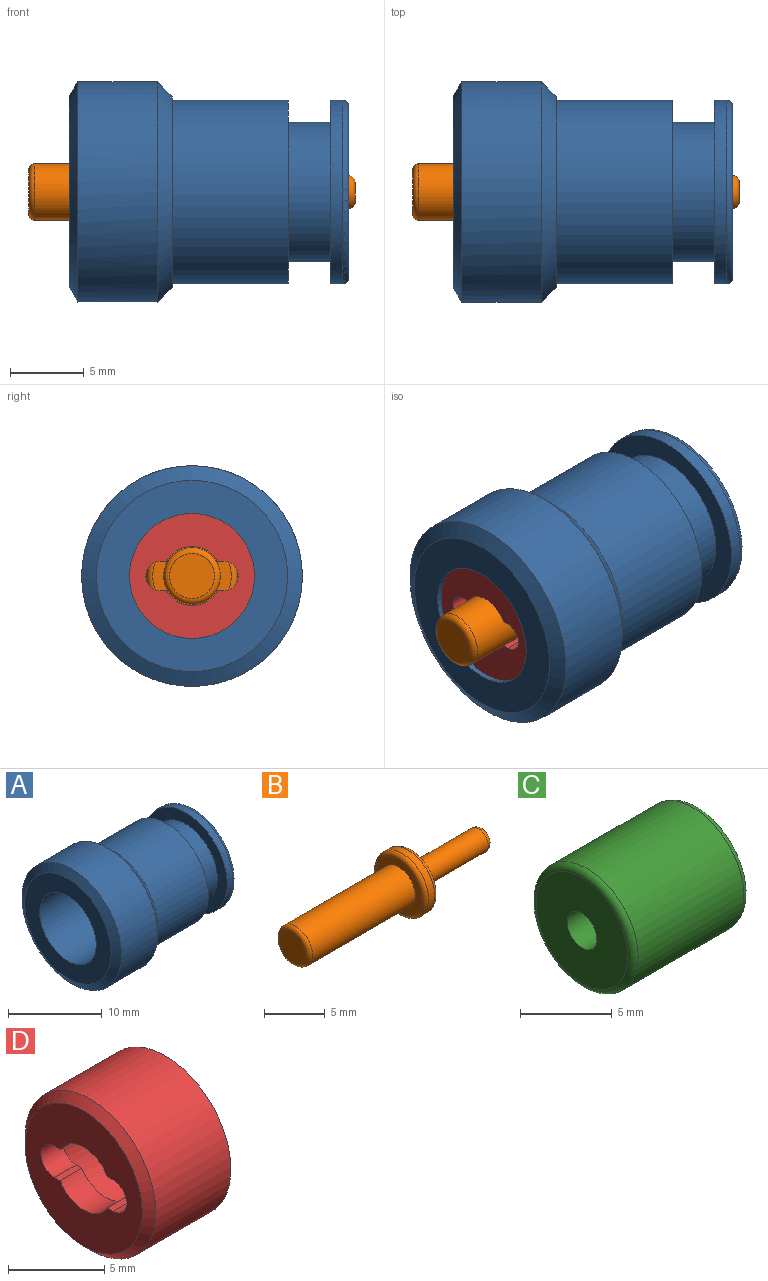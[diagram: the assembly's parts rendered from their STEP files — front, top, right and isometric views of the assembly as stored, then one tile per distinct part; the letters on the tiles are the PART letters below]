
ASSEMBLY  parts=4 mates=3
PART A: 19 faces, bbox 19x15x15 mm
  f0: plane 13x13mm, normal (-1,0,0), area 76mm2, adj f1,f16
  f1: cylinder r=4.25mm len=8.5mm, axis (-1,0,0), area 213.6mm2, adj f0,f2
  f2: plane 8.5x8.5mm, normal (-1,0,0), area 6.5mm2, adj f1,f3
  f3: cylinder r=4mm len=8mm, axis (-1,0,0), area 193.5mm2, adj f2,f4
  f4: plane 8x8mm, normal (-1,0,0), area 23.8mm2, adj f3,f5
  f5: cylinder r=2.9mm len=5.8mm, axis (-1,0,0), area 32.8mm2, adj f4,f6
  f6: plane 5.8x5.8mm, normal (-1,0,0), area 21.9mm2, adj f5,f7
  f7: cylinder r=1.2mm len=2.4mm, axis (-1,0,0), area 11.3mm2, adj f6,f8
  f8: plane 11.68x11.68mm, normal (1,0,0), area 102.5mm2, adj f7,f18
  f9: cylinder r=6.24mm len=12.48mm, axis (-1,0,0), area 33.3mm2, adj f10,f18
  f10: plane 12.48x12.48mm, normal (-1,0,0), area 51.6mm2, adj f9,f11
  f11: cylinder r=4.74mm len=9.48mm, axis (-1,0,0), area 84.9mm2, adj f10,f12
  f12: plane 12.48x12.48mm, normal (1,0,0), area 51.6mm2, adj f11,f13
  f13: cylinder r=6.24mm len=12.48mm, axis (-1,0,0), area 309.6mm2, adj f12,f14
  f14: plane 13x13mm, normal (1,0,0), area 10.5mm2, adj f13,f17
  f15: cylinder r=7.5mm len=15mm, axis (-1,0,0), area 255.5mm2, adj f16,f17
  f16: cone r=6.5mm half-angle=60deg, axis (1,0,0), area 50.8mm2, adj f0,f15
  f17: cone r=7.5mm half-angle=45deg, axis (-1,0,0), area 62.2mm2, adj f14,f15
  f18: torus R=5.84mm, axis (1,0,0), area 24.1mm2, adj f8,f9
PART B: 11 faces, bbox 22.2x6.7x6.7 mm
  f0: plane 1.27x1.27mm, normal (1,0,0), area 1.3mm2, adj f1
  f1: torus R=0.63mm, axis (1,0,0), area 4.7mm2, adj f0,f2
  f2: cylinder r=1.13mm len=7.8mm, axis (1,0,0), area 55.5mm2, adj f1,f3
  f3: plane 5.35x5.35mm, normal (1,0,0), area 18.4mm2, adj f2,f4
  f4: torus R=2.67mm, axis (1,0,0), area 11.6mm2, adj f3,f5
  f5: cylinder r=3.08mm len=6.15mm, axis (1,0,0), area 13.5mm2, adj f4,f6
  f6: torus R=2.67mm, axis (1,0,0), area 11.6mm2, adj f5,f7
  f7: plane 5.35x5.35mm, normal (-1,0,0), area 10.8mm2, adj f6,f8
  f8: cylinder r=1.93mm len=12mm, axis (1,0,0), area 145.1mm2, adj f7,f9
  f9: torus R=1.53mm, axis (1,0,0), area 7mm2, adj f8,f10
  f10: plane 3.05x3.05mm, normal (-1,0,0), area 7.3mm2, adj f9
PART C: 8 faces, bbox 8.9x8.5x8.5 mm
  f0: plane 7.05x7.05mm, normal (-1,0,0), area 34.9mm2, adj f1,f7
  f1: cylinder r=1.15mm len=2.3mm, axis (1,0,0), area 12mm2, adj f0,f2
  f2: plane 6.3x6.3mm, normal (1,0,0), area 27mm2, adj f1,f3
  f3: cylinder r=3.15mm len=7.28mm, axis (1,0,0), area 144.1mm2, adj f2,f4
  f4: plane 7.05x7.05mm, normal (1,0,0), area 7.9mm2, adj f3,f5
  f5: torus R=3.53mm, axis (1,0,0), area 14.9mm2, adj f4,f6
  f6: cylinder r=3.93mm len=8.14mm, axis (1,0,0), area 200.8mm2, adj f5,f7
  f7: torus R=3.53mm, axis (1,0,0), area 14.9mm2, adj f0,f6
PART D: 15 faces, bbox 6.4x9.6x9.6 mm
  f0: plane 8.6x8.6mm, normal (-1,0,0), area 41.4mm2, adj f1,f2,f8,f9,f10,f11,f12,f13
  f1: cylinder r=2mm len=3.46mm, axis (1,0,0), area 6.7mm2, adj f0,f5,f10,f11
  f2: cylinder r=2mm len=3.46mm, axis (1,0,0), area 6.7mm2, adj f0,f5,f9,f13
  f3: cone r=4.8mm half-angle=60deg, axis (-1,0,0), area 22mm2, adj f4,f7
  f4: cylinder r=4.8mm len=9.6mm, axis (1,0,0), area 166.1mm2, adj f3,f14
  f5: plane 6.33x6.33mm, normal (1,0,0), area 14.8mm2, adj f1,f2,f6,f8,f9,f10,f11,f12
  f6: cylinder r=3.16mm len=6.33mm, axis (1,0,0), area 95.4mm2, adj f5,f7
  f7: plane 8.24x8.24mm, normal (1,0,0), area 21.9mm2, adj f3,f6
  f8: cylinder r=1mm len=2mm, axis (-1,0,0), area 5mm2, adj f0,f5,f9,f10
  f9: plane 1.6x0.42mm, normal (0,0,-1), area 0.7mm2, adj f0,f2,f5,f8
  f10: plane 1.6x0.42mm, normal (0,0,1), area 0.7mm2, adj f0,f1,f5,f8
  f11: plane 1.6x0.42mm, normal (0,0,1), area 0.7mm2, adj f0,f1,f5,f12
  f12: cylinder r=1mm len=2mm, axis (-1,0,0), area 5mm2, adj f0,f5,f11,f13
  f13: plane 1.6x0.42mm, normal (0,0,-1), area 0.7mm2, adj f0,f2,f5,f12
  f14: cone r=4.3mm half-angle=45deg, axis (1,0,0), area 20.2mm2, adj f0,f4
PLACE A t=(11.17,7,-7.4)mm
PLACE B t=(8.42,7,-7.4)mm
PLACE C rot(axis=(0,1,0),180deg) t=(26.87,7,-7.4)mm
PLACE D t=(11.53,7,-7.4)mm
MATE fastened C.f1 <-> A.f1  axis (1,0,0) through (26.87,7,-7.4)mm
MATE cylindrical B.f1 <-> C.f1  axis (1,0,0) through (21.57,7,-7.4)mm
MATE fastened D.f1 <-> C.f1  axis (1,0,0) through (17.93,7,-7.4)mm
